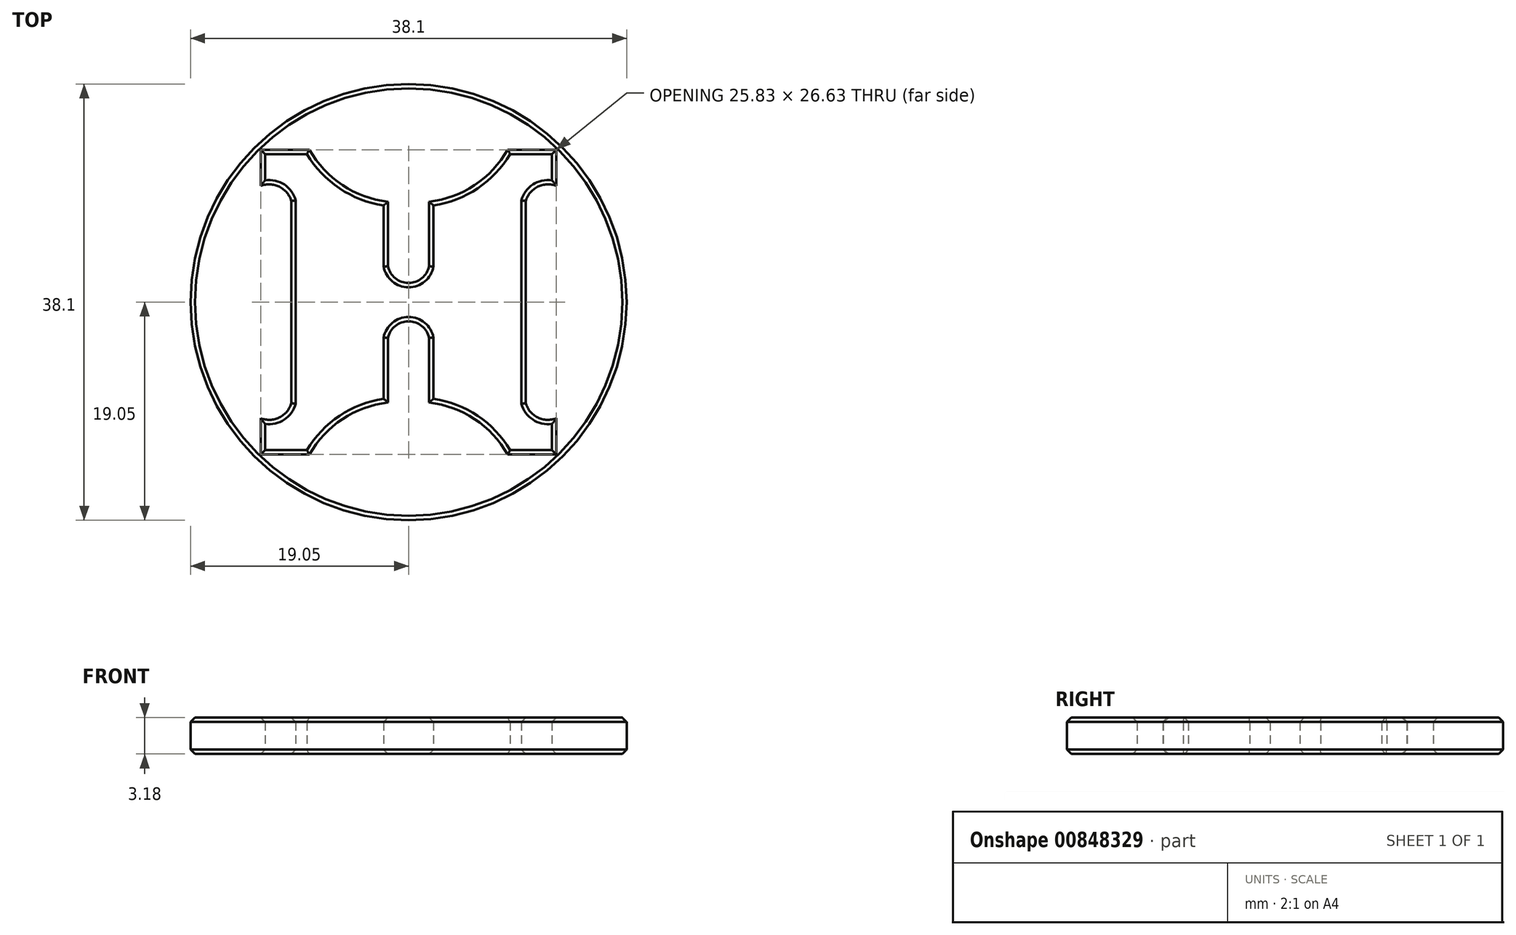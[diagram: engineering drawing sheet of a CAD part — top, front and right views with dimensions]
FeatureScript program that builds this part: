
annotation { "Feature Type Name" : "Feature", "Feature Type Description" : "" }
export const myFeature = defineFeature(function(context is Context, id is Id, definition is map)
    precondition{}
    {
        {
            var Q0;
            Q0=qCreatedBy(makeId("Top.planeOp"),FACE);
            var sketch = newSketch(context, id + "F0", { "sketchPlane" : qUnion([Q0])});
            skCircle(sketch, "E0", {"center": v(0, 0) * mm, "radius": 19.05 * mm});
            skPoint(sketch, "E1.endSnap0", {"position": v(-7.25, -1.1) * mm});
            skPoint(sketch, "E2.startSnap0", {"position": v(0, -4.76) * mm});
            skArc(sketch, "E3", {"start": v(-12.53, -10.64) * mm, "mid": v(-10.86, -10.27) * mm, "end": v(-9.86, -8.88) * mm});
            skLineSegment(sketch, "E4", {"start": v(-12.53, -10.64) * mm, "end": v(-12.53, -12.93) * mm});
            skArc(sketch, "E5.MirrorCS", {"start": v(12.53, -10.64) * mm, "mid": v(10.86, -10.27) * mm, "end": v(9.86, -8.88) * mm});
            skLineSegment(sketch, "E6.MirrorCS", {"start": v(12.53, -10.64) * mm, "end": v(12.53, -12.93) * mm});
            skArc(sketch, "E7", {"start": v(-2.18, -8.44) * mm, "mid": v(-6.03, -9.94) * mm, "end": v(-8.88, -12.93) * mm});
            skArc(sketch, "E8.MirrorCS", {"start": v(2.18, -8.44) * mm, "mid": v(6.03, -9.94) * mm, "end": v(8.88, -12.93) * mm});
            skLineSegment(sketch, "E9", {"start": v(-12.53, -12.93) * mm, "end": v(-8.88, -12.93) * mm});
            skLineSegment(sketch, "E10", {"start": v(8.88, -12.93) * mm, "end": v(12.53, -12.93) * mm});
            skArc(sketch, "E11.MirrorCS", {"start": v(-2.18, -3.1) * mm, "mid": v(0, -1.3) * mm, "end": v(2.18, -3.1) * mm});
            skLineSegment(sketch, "E12", {"start": v(-2.18, -3.1) * mm, "end": v(-2.18, -8.44) * mm});
            skLineSegment(sketch, "E13", {"start": v(2.18, -3.1) * mm, "end": v(2.18, -8.44) * mm});
            skArc(sketch, "E14.MirrorCS", {"start": v(-2.18, 3.1) * mm, "mid": v(0, 1.3) * mm, "end": v(2.18, 3.1) * mm});
            skLineSegment(sketch, "E15.MirrorCS", {"start": v(2.18, 3.1) * mm, "end": v(2.18, 8.44) * mm});
            skLineSegment(sketch, "E16.MirrorCS", {"start": v(-2.18, 3.1) * mm, "end": v(-2.18, 8.44) * mm});
            skArc(sketch, "E17.MirrorCS", {"start": v(-2.18, 8.44) * mm, "mid": v(-6.03, 9.94) * mm, "end": v(-8.88, 12.93) * mm});
            skArc(sketch, "E18.MirrorCS", {"start": v(2.18, 8.44) * mm, "mid": v(6.03, 9.94) * mm, "end": v(8.88, 12.93) * mm});
            skLineSegment(sketch, "E19.MirrorCS", {"start": v(8.88, 12.93) * mm, "end": v(12.53, 12.93) * mm});
            skLineSegment(sketch, "E20.MirrorCS", {"start": v(12.53, 10.64) * mm, "end": v(12.53, 12.93) * mm});
            skArc(sketch, "E21.MirrorCS", {"start": v(12.53, 10.64) * mm, "mid": v(10.86, 10.27) * mm, "end": v(9.86, 8.88) * mm});
            skLineSegment(sketch, "E22.MirrorCS", {"start": v(-12.53, 12.93) * mm, "end": v(-8.88, 12.93) * mm});
            skLineSegment(sketch, "E23.MirrorCS", {"start": v(-12.53, 10.64) * mm, "end": v(-12.53, 12.93) * mm});
            skArc(sketch, "E24.MirrorCS", {"start": v(-12.53, 10.64) * mm, "mid": v(-10.86, 10.27) * mm, "end": v(-9.86, 8.88) * mm});
            skLineSegment(sketch, "E25", {"start": v(-9.86, 8.88) * mm, "end": v(-9.86, -8.88) * mm});
            skLineSegment(sketch, "E26", {"start": v(9.86, 8.88) * mm, "end": v(9.86, -8.88) * mm});
            skSolve(sketch);
        }
        {
            var Q0;
            Q0=makeQuery(id+"F0.imprint","IMPRINT",FACE,{"disambiguationData":[TD([[makeQuery(id+"F0.imprint","IMPRINT",EDGE,{"derivedFrom":sQuery(id+"F0.wireOp",EDGE,"E0")}),1.0]])]});
            extrude(context, id + "F1", {"entities" : qUnion([Q0]), "depth" : 3.17 * mm, "offsetDistance" : 25.4 * mm});
        }
        {
            var Q0;
            Q0=makeQuery(id+"F1.opExtrude","CAP_EDGE",EDGE,{"disambiguationData":[OSD([sQuery(id+"F0.wireOp",EDGE,"E22.MirrorCS")])],"isStart":false});
            var Q1;
            Q1=makeQuery(id+"F1.opExtrude","CAP_EDGE",EDGE,{"disambiguationData":[OSD([sQuery(id+"F0.wireOp",EDGE,"E23.MirrorCS")])],"isStart":false});
            var Q2;
            Q2=makeQuery(id+"F1.opExtrude","CAP_EDGE",EDGE,{"disambiguationData":[OSD([sQuery(id+"F0.wireOp",EDGE,"E23.MirrorCS")])],"isStart":true});
            var Q3;
            Q3=makeQuery(id+"F1.opExtrude","CAP_EDGE",EDGE,{"disambiguationData":[OSD([sQuery(id+"F0.wireOp",EDGE,"E22.MirrorCS")])],"isStart":true});
            var Q4;
            Q4=makeQuery(id+"F1.opExtrude","CAP_EDGE",EDGE,{"disambiguationData":[OSD([sQuery(id+"F0.wireOp",EDGE,"E17.MirrorCS")])],"isStart":false});
            var Q5;
            Q5=makeQuery(id+"F1.opExtrude","CAP_EDGE",EDGE,{"disambiguationData":[OSD([sQuery(id+"F0.wireOp",EDGE,"E17.MirrorCS")])],"isStart":true});
            var Q6;
            Q6=makeQuery(id+"F1.opExtrude","CAP_EDGE",EDGE,{"disambiguationData":[OSD([sQuery(id+"F0.wireOp",EDGE,"E16.MirrorCS")])],"isStart":true});
            var Q7;
            Q7=makeQuery(id+"F1.opExtrude","CAP_EDGE",EDGE,{"disambiguationData":[OSD([sQuery(id+"F0.wireOp",EDGE,"E16.MirrorCS")])],"isStart":false});
            var Q8;
            Q8=makeQuery(id+"F1.opExtrude","CAP_EDGE",EDGE,{"disambiguationData":[OSD([sQuery(id+"F0.wireOp",EDGE,"E14.MirrorCS")])],"isStart":false});
            var Q9;
            Q9=makeQuery(id+"F1.opExtrude","CAP_EDGE",EDGE,{"disambiguationData":[OSD([sQuery(id+"F0.wireOp",EDGE,"E14.MirrorCS")])],"isStart":true});
            var Q10;
            Q10=makeQuery(id+"F1.opExtrude","CAP_EDGE",EDGE,{"disambiguationData":[OSD([sQuery(id+"F0.wireOp",EDGE,"E24.MirrorCS")])],"isStart":true});
            var Q11;
            Q11=makeQuery(id+"F1.opExtrude","CAP_EDGE",EDGE,{"disambiguationData":[OSD([sQuery(id+"F0.wireOp",EDGE,"E24.MirrorCS")])],"isStart":false});
            var Q12;
            Q12=makeQuery(id+"F1.opExtrude","CAP_EDGE",EDGE,{"disambiguationData":[OSD([sQuery(id+"F0.wireOp",EDGE,"E25")])],"isStart":true});
            var Q13;
            Q13=makeQuery(id+"F1.opExtrude","CAP_EDGE",EDGE,{"disambiguationData":[OSD([sQuery(id+"F0.wireOp",EDGE,"E25")])],"isStart":false});
            var Q14;
            Q14=makeQuery(id+"F1.opExtrude","CAP_EDGE",EDGE,{"disambiguationData":[OSD([sQuery(id+"F0.wireOp",EDGE,"E15.MirrorCS")])],"isStart":true});
            var Q15;
            Q15=makeQuery(id+"F1.opExtrude","CAP_EDGE",EDGE,{"disambiguationData":[OSD([sQuery(id+"F0.wireOp",EDGE,"E15.MirrorCS")])],"isStart":false});
            var Q16;
            Q16=makeQuery(id+"F1.opExtrude","CAP_EDGE",EDGE,{"disambiguationData":[OSD([sQuery(id+"F0.wireOp",EDGE,"E11.MirrorCS")])],"isStart":true});
            var Q17;
            Q17=makeQuery(id+"F1.opExtrude","CAP_EDGE",EDGE,{"disambiguationData":[OSD([sQuery(id+"F0.wireOp",EDGE,"E11.MirrorCS")])],"isStart":false});
            var Q18;
            Q18=makeQuery(id+"F1.opExtrude","CAP_EDGE",EDGE,{"disambiguationData":[OSD([sQuery(id+"F0.wireOp",EDGE,"E12")])],"isStart":true});
            var Q19;
            Q19=makeQuery(id+"F1.opExtrude","CAP_EDGE",EDGE,{"disambiguationData":[OSD([sQuery(id+"F0.wireOp",EDGE,"E12")])],"isStart":false});
            var Q20;
            Q20=makeQuery(id+"F1.opExtrude","CAP_EDGE",EDGE,{"disambiguationData":[OSD([sQuery(id+"F0.wireOp",EDGE,"E7")])],"isStart":true});
            var Q21;
            Q21=makeQuery(id+"F1.opExtrude","CAP_EDGE",EDGE,{"disambiguationData":[OSD([sQuery(id+"F0.wireOp",EDGE,"E7")])],"isStart":false});
            var Q22;
            Q22=makeQuery(id+"F1.opExtrude","CAP_EDGE",EDGE,{"disambiguationData":[OSD([sQuery(id+"F0.wireOp",EDGE,"E9")])],"isStart":true});
            var Q23;
            Q23=makeQuery(id+"F1.opExtrude","CAP_EDGE",EDGE,{"disambiguationData":[OSD([sQuery(id+"F0.wireOp",EDGE,"E9")])],"isStart":false});
            var Q24;
            Q24=makeQuery(id+"F1.opExtrude","CAP_EDGE",EDGE,{"disambiguationData":[OSD([sQuery(id+"F0.wireOp",EDGE,"E4")])],"isStart":true});
            var Q25;
            Q25=makeQuery(id+"F1.opExtrude","CAP_EDGE",EDGE,{"disambiguationData":[OSD([sQuery(id+"F0.wireOp",EDGE,"E4")])],"isStart":false});
            var Q26;
            Q26=makeQuery(id+"F1.opExtrude","CAP_EDGE",EDGE,{"disambiguationData":[OSD([sQuery(id+"F0.wireOp",EDGE,"E3")])],"isStart":false});
            var Q27;
            Q27=makeQuery(id+"F1.opExtrude","CAP_EDGE",EDGE,{"disambiguationData":[OSD([sQuery(id+"F0.wireOp",EDGE,"E3")])],"isStart":true});
            var Q28;
            Q28=makeQuery(id+"F1.opExtrude","CAP_EDGE",EDGE,{"disambiguationData":[OSD([sQuery(id+"F0.wireOp",EDGE,"E13")])],"isStart":true});
            var Q29;
            Q29=makeQuery(id+"F1.opExtrude","CAP_EDGE",EDGE,{"disambiguationData":[OSD([sQuery(id+"F0.wireOp",EDGE,"E13")])],"isStart":false});
            var Q30;
            Q30=makeQuery(id+"F1.opExtrude","CAP_EDGE",EDGE,{"disambiguationData":[OSD([sQuery(id+"F0.wireOp",EDGE,"E8.MirrorCS")])],"isStart":true});
            var Q31;
            Q31=makeQuery(id+"F1.opExtrude","CAP_EDGE",EDGE,{"disambiguationData":[OSD([sQuery(id+"F0.wireOp",EDGE,"E8.MirrorCS")])],"isStart":false});
            var Q32;
            Q32=makeQuery(id+"F1.opExtrude","CAP_EDGE",EDGE,{"disambiguationData":[OSD([sQuery(id+"F0.wireOp",EDGE,"E10")])],"isStart":true});
            var Q33;
            Q33=makeQuery(id+"F1.opExtrude","CAP_EDGE",EDGE,{"disambiguationData":[OSD([sQuery(id+"F0.wireOp",EDGE,"E10")])],"isStart":false});
            var Q34;
            Q34=makeQuery(id+"F1.opExtrude","CAP_EDGE",EDGE,{"disambiguationData":[OSD([sQuery(id+"F0.wireOp",EDGE,"E6.MirrorCS")])],"isStart":false});
            var Q35;
            Q35=makeQuery(id+"F1.opExtrude","CAP_EDGE",EDGE,{"disambiguationData":[OSD([sQuery(id+"F0.wireOp",EDGE,"E6.MirrorCS")])],"isStart":true});
            var Q36;
            Q36=makeQuery(id+"F1.opExtrude","CAP_EDGE",EDGE,{"disambiguationData":[OSD([sQuery(id+"F0.wireOp",EDGE,"E5.MirrorCS")])],"isStart":false});
            var Q37;
            Q37=makeQuery(id+"F1.opExtrude","CAP_EDGE",EDGE,{"disambiguationData":[OSD([sQuery(id+"F0.wireOp",EDGE,"E5.MirrorCS")])],"isStart":true});
            var Q38;
            Q38=makeQuery(id+"F1.opExtrude","CAP_EDGE",EDGE,{"disambiguationData":[OSD([sQuery(id+"F0.wireOp",EDGE,"E26")])],"isStart":true});
            var Q39;
            Q39=makeQuery(id+"F1.opExtrude","CAP_EDGE",EDGE,{"disambiguationData":[OSD([sQuery(id+"F0.wireOp",EDGE,"E26")])],"isStart":false});
            var Q40;
            Q40=makeQuery(id+"F1.opExtrude","CAP_EDGE",EDGE,{"disambiguationData":[OSD([sQuery(id+"F0.wireOp",EDGE,"E21.MirrorCS")])],"isStart":false});
            var Q41;
            Q41=makeQuery(id+"F1.opExtrude","CAP_EDGE",EDGE,{"disambiguationData":[OSD([sQuery(id+"F0.wireOp",EDGE,"E21.MirrorCS")])],"isStart":true});
            var Q42;
            Q42=makeQuery(id+"F1.opExtrude","CAP_EDGE",EDGE,{"disambiguationData":[OSD([sQuery(id+"F0.wireOp",EDGE,"E20.MirrorCS")])],"isStart":false});
            var Q43;
            Q43=makeQuery(id+"F1.opExtrude","CAP_EDGE",EDGE,{"disambiguationData":[OSD([sQuery(id+"F0.wireOp",EDGE,"E20.MirrorCS")])],"isStart":true});
            var Q44;
            Q44=makeQuery(id+"F1.opExtrude","CAP_EDGE",EDGE,{"disambiguationData":[OSD([sQuery(id+"F0.wireOp",EDGE,"E19.MirrorCS")])],"isStart":false});
            var Q45;
            Q45=makeQuery(id+"F1.opExtrude","CAP_EDGE",EDGE,{"disambiguationData":[OSD([sQuery(id+"F0.wireOp",EDGE,"E19.MirrorCS")])],"isStart":true});
            var Q46;
            Q46=makeQuery(id+"F1.opExtrude","CAP_EDGE",EDGE,{"disambiguationData":[OSD([sQuery(id+"F0.wireOp",EDGE,"E18.MirrorCS")])],"isStart":true});
            var Q47;
            Q47=makeQuery(id+"F1.opExtrude","CAP_EDGE",EDGE,{"disambiguationData":[OSD([sQuery(id+"F0.wireOp",EDGE,"E18.MirrorCS")])],"isStart":false});
            chamfer(context, id + "F2", {"entities" : qUnion([Q0, Q1, Q2, Q3, Q4, Q5, Q6, Q7, Q8, Q9, Q10, Q11, Q12, Q13, Q14, Q15, Q16, Q17, Q18, Q19, Q20, Q21, Q22, Q23, Q24, Q25, Q26, Q27, Q28, Q29, Q30, Q31, Q32, Q33, Q34, Q35, Q36, Q37, Q38, Q39, Q40, Q41, Q42, Q43, Q44, Q45, Q46, Q47]), "width" : 0.38 * mm, "tangentPropagation" : true});
        }
        {
            var Q0;
            Q0=makeQuery(id+"F1.opExtrude","CAP_EDGE",EDGE,{"disambiguationData":[OSD([sQuery(id+"F0.wireOp",EDGE,"E0")])],"isStart":true});
            var Q1;
            Q1=makeQuery(id+"F1.opExtrude","CAP_EDGE",EDGE,{"disambiguationData":[OSD([sQuery(id+"F0.wireOp",EDGE,"E0")])],"isStart":false});
            chamfer(context, id + "F3", {"entities" : qUnion([Q0, Q1]), "width" : 0.38 * mm, "tangentPropagation" : true});
        }
    });
